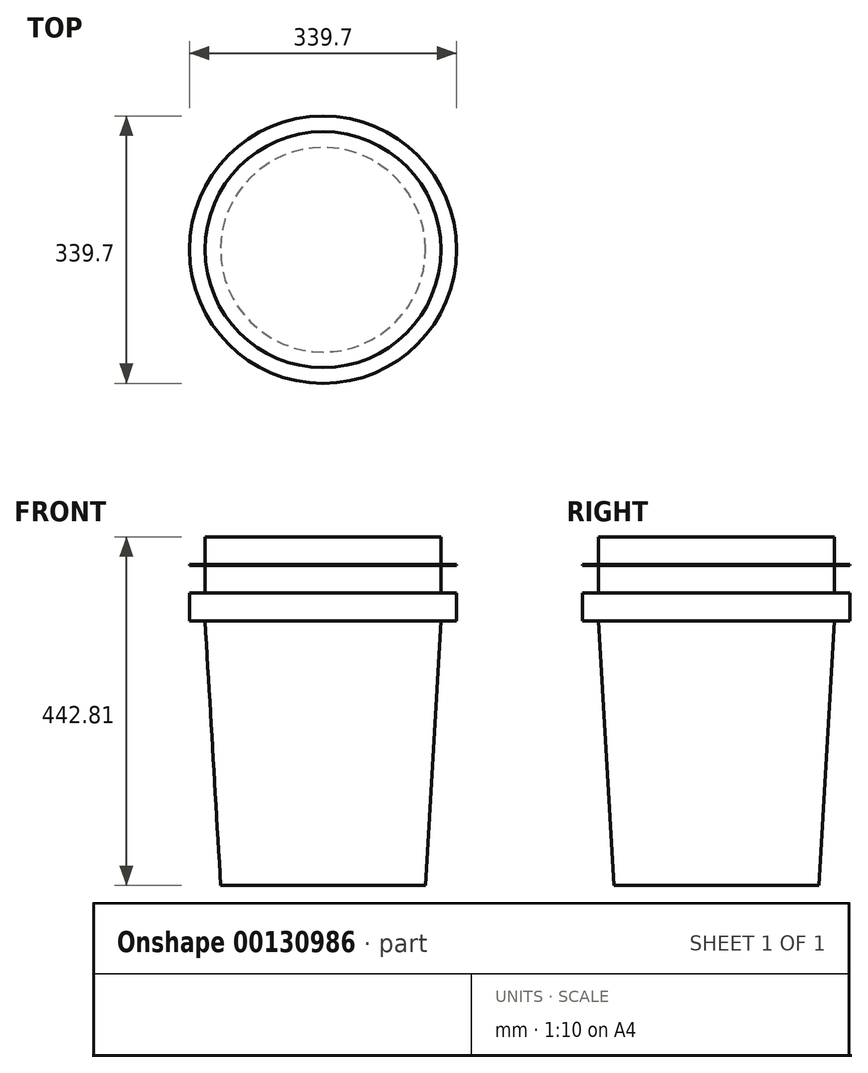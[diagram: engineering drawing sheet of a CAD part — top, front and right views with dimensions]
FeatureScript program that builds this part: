
annotation { "Feature Type Name" : "Feature", "Feature Type Description" : "" }
export const myFeature = defineFeature(function(context is Context, id is Id, definition is map)
    precondition{}
    {
        {
            var Q0;
            Q0=qCreatedBy(makeId("Front.planeOp"),FACE);
            var sketch = newSketch(context, id + "F0", { "sketchPlane" : qUnion([Q0])});
            skLineSegment(sketch, "E0", {"start": v(0, 0) * mm, "end": v(130, 0) * mm});
            skLineSegment(sketch, "E1", {"start": v(0, 0) * mm, "end": v(0, 336.1) * mm});
            skLineSegment(sketch, "E2", {"start": v(0, 336.1) * mm, "end": v(149.85, 336.1) * mm});
            skLineSegment(sketch, "E3", {"start": v(130, 0) * mm, "end": v(149.85, 336.1) * mm});
            skLineSegment(sketch, "E4", {"start": v(0, 336.1) * mm, "end": v(0, 371.67) * mm});
            skLineSegment(sketch, "E5", {"start": v(0, 371.67) * mm, "end": v(169.85, 371.67) * mm});
            skLineSegment(sketch, "E6", {"start": v(169.85, 371.67) * mm, "end": v(169.85, 336.1) * mm});
            skLineSegment(sketch, "E7", {"start": v(169.85, 336.1) * mm, "end": v(149.85, 336.1) * mm});
            skLineSegment(sketch, "E8", {"start": v(0, 371.67) * mm, "end": v(0, 406.74) * mm});
            skLineSegment(sketch, "E9", {"start": v(0, 406.74) * mm, "end": v(149.85, 406.74) * mm});
            skLineSegment(sketch, "E10", {"start": v(149.85, 406.74) * mm, "end": v(149.85, 371.67) * mm});
            skLineSegment(sketch, "E11", {"start": v(0, 406.74) * mm, "end": v(0, 407.74) * mm});
            skLineSegment(sketch, "E12", {"start": v(0, 407.74) * mm, "end": v(169.85, 407.74) * mm});
            skLineSegment(sketch, "E13", {"start": v(169.85, 407.74) * mm, "end": v(169.85, 406.74) * mm});
            skLineSegment(sketch, "E14", {"start": v(169.85, 406.74) * mm, "end": v(149.85, 406.74) * mm});
            skLineSegment(sketch, "E15", {"start": v(0, 407.74) * mm, "end": v(0, 442.8) * mm});
            skLineSegment(sketch, "E16", {"start": v(0, 442.8) * mm, "end": v(149.85, 442.8) * mm});
            skLineSegment(sketch, "E17", {"start": v(149.85, 442.8) * mm, "end": v(149.85, 407.74) * mm});
            skSolve(sketch);
        }
        {
            var Q0;
            Q0 = qSketchRegion(id + "F0", true);
            var Q1;
            Q1=sQuery(id+"F0.wireOp",EDGE,"E1");
            revolve(context, id + "F1", {"entities" : qUnion([Q0]), "axis" : qUnion([Q1]), "revolveType" : RevolveType.FULL});
        }
    });
